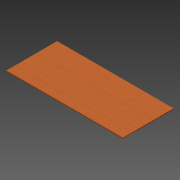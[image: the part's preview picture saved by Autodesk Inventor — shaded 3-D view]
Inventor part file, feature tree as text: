
AUTODESK INVENTOR PART (.ipt)
format: ipt  version: 2013 (Build 170138000, 138)  size: 75,264 bytes
history: native  units: in
note: dims shown in document units (in); Inventor stores cm internally (conversion verified against a paired STEP export)
features: extrude x1, sketch x1
ambient origin geometry x8: Origin, YZ Plane, XZ Plane, XY Plane, X Axis, Y Axis, Z Axis, Center Point
bodies: Solid1 (feature_tree)
feature tree (2):
  extrude  "Extrusion1"  Depth=24.0in
  sketch  "Sketch1"  dims[d0=55.0in d1=24.0in d2=0.5in d3=0.0in]
